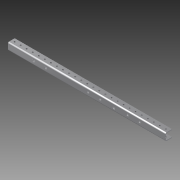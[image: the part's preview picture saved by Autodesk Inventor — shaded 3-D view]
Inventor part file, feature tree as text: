
AUTODESK INVENTOR PART (.ipt)
format: ipt  version: 2013 (Build 170138000, 138)  size: 193,024 bytes
history: native  units: in
note: dims shown in document units (in); Inventor stores cm internally (conversion verified against a paired STEP export)
features: sketch x4, hole x3, extrude x2, pattern_linear x1
ambient origin geometry x8: Origin, YZ Plane, XZ Plane, XY Plane, X Axis, Y Axis, Z Axis, Center Point
bodies: Solid1 (feature_tree)
feature tree (10):
  extrude  "Extrusion1"  Depth=0.125in
  sketch  "Sketch2"  dims[d2=1.0in d3=1.0in]
  hole  "Hole1"  [1 undecoded]
  hole  "Hole2"  [1 undecoded]
  hole  "Hole3"  [1 undecoded]
  pattern_linear  "Rectangular Pattern1"  Spacing1=0.3in  [1 undecoded]
  extrude  "Extrusion2"  Depth=0.15in
  sketch  "Sketch1"  dims[d0=1.125in d1=0.125in]
  sketch  "Sketch3"  dims[d4=0.125in d5=0.125in]
  sketch  "Sketch4"  dims[d6=0.25in d7=35.0in d8=0.0in d10=0.3in d11=0.15in d12=0.7874in d14=10.0in d15=0.3937in d17=1.0in d20=0.38in d21=0.75in d22=0.375in d23=0.25in d24=0.5635in d25=1.0in d26=0.8108in d27=0.125in d28=0.75in d29=0.375in d30=0.25in d31=0.5635in d32=1.0in d33=0.8108in d34=0.5in d35=0.5in d36=0.257in d37=0.75in d38=0.375in d39=0.25in d40=0.5635in d41=1.0in d42=0.8108in d43=13.7795in d45=1.0in d46=9.0in d47=0.0in]
note: 4 required parameter values undecoded (feature->parameter linkage not recoverable at this tier; creation-order binding heuristic only, values carry confidence <= 0.55)
